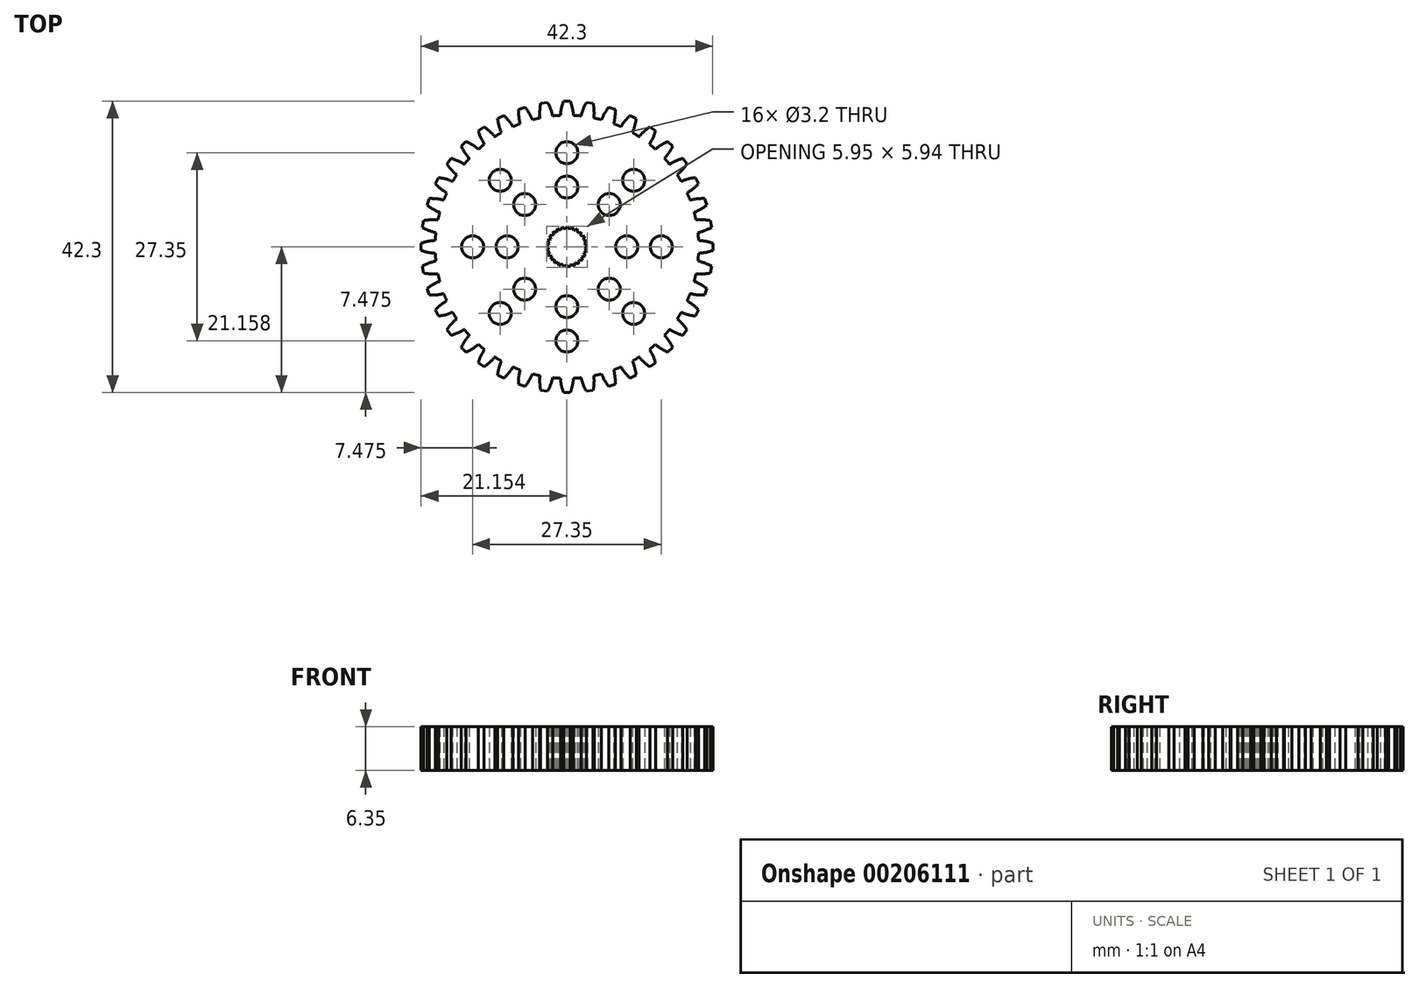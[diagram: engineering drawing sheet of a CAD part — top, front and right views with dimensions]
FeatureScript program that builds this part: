
annotation { "Feature Type Name" : "Feature", "Feature Type Description" : "" }
export const myFeature = defineFeature(function(context is Context, id is Id, definition is map)
    precondition{}
    {
        {
            var Q0;
            Q0=qCreatedBy(makeId("Top.planeOp"),FACE);
            var sketch = newSketch(context, id + "F0", { "sketchPlane" : qUnion([Q0])});
            skLineSegment(sketch, "E0", {"start": v(-0.5, 21.15) * mm, "end": v(0.5, 21.15) * mm});
            skArc(sketch, "E1", {"start": v(-0.5, 21.15) * mm, "mid": v(-0.8, 20.14) * mm, "end": v(-0.94, 19.09) * mm});
            skArc(sketch, "E2.MirrorCS", {"start": v(0.5, 21.15) * mm, "mid": v(0.8, 20.14) * mm, "end": v(0.94, 19.09) * mm});
            skPoint(sketch, "E3.center", {"position": v(0, 0) * mm});
            skLineSegment(sketch, "E4", {"start": v(-2.48, 1.65) * mm, "end": v(-2.31, 1.15) * mm});
            skLineSegment(sketch, "E5", {"start": v(-2.31, 1.15) * mm, "end": v(-2.81, 0.98) * mm});
            skLineSegment(sketch, "E6.1.0", {"start": v(-2.81, 0.98) * mm, "end": v(-2.53, 0.54) * mm});
            skLineSegment(sketch, "E6.1.1", {"start": v(-2.53, 0.54) * mm, "end": v(-2.97, 0.25) * mm});
            skLineSegment(sketch, "E6.2.0", {"start": v(-2.97, 0.25) * mm, "end": v(-2.58, -0.1) * mm});
            skLineSegment(sketch, "E6.2.1", {"start": v(-2.58, -0.1) * mm, "end": v(-2.94, -0.5) * mm});
            skLineSegment(sketch, "E6.3.0", {"start": v(-2.94, -0.5) * mm, "end": v(-2.47, -0.74) * mm});
            skLineSegment(sketch, "E6.3.1", {"start": v(-2.47, -0.74) * mm, "end": v(-2.72, -1.2) * mm});
            skLineSegment(sketch, "E6.4.0", {"start": v(-2.72, -1.2) * mm, "end": v(-2.21, -1.34) * mm});
            skLineSegment(sketch, "E6.4.1", {"start": v(-2.21, -1.34) * mm, "end": v(-2.34, -1.85) * mm});
            skLineSegment(sketch, "E6.5.0", {"start": v(-2.34, -1.85) * mm, "end": v(-1.8, -1.84) * mm});
            skLineSegment(sketch, "E6.5.1", {"start": v(-1.8, -1.84) * mm, "end": v(-1.8, -2.37) * mm});
            skLineSegment(sketch, "E6.6.0", {"start": v(-1.8, -2.37) * mm, "end": v(-1.3, -2.24) * mm});
            skLineSegment(sketch, "E6.6.1", {"start": v(-1.3, -2.24) * mm, "end": v(-1.16, -2.75) * mm});
            skLineSegment(sketch, "E6.7.0", {"start": v(-1.16, -2.75) * mm, "end": v(-0.7, -2.49) * mm});
            skLineSegment(sketch, "E6.7.1", {"start": v(-0.7, -2.49) * mm, "end": v(-0.44, -2.95) * mm});
            skLineSegment(sketch, "E6.8.0", {"start": v(-0.44, -2.95) * mm, "end": v(-0.06, -2.58) * mm});
            skLineSegment(sketch, "E6.8.1", {"start": v(-0.06, -2.58) * mm, "end": v(0.3, -2.96) * mm});
            skLineSegment(sketch, "E6.9.0", {"start": v(0.3, -2.96) * mm, "end": v(0.59, -2.52) * mm});
            skLineSegment(sketch, "E6.9.1", {"start": v(0.59, -2.52) * mm, "end": v(1.04, -2.8) * mm});
            skLineSegment(sketch, "E6.10.0", {"start": v(1.04, -2.8) * mm, "end": v(1.2, -2.3) * mm});
            skLineSegment(sketch, "E6.10.1", {"start": v(1.2, -2.3) * mm, "end": v(1.7, -2.45) * mm});
            skLineSegment(sketch, "E6.11.0", {"start": v(1.7, -2.45) * mm, "end": v(1.73, -1.92) * mm});
            skLineSegment(sketch, "E6.11.1", {"start": v(1.73, -1.92) * mm, "end": v(2.25, -1.95) * mm});
            skLineSegment(sketch, "E6.12.0", {"start": v(2.25, -1.95) * mm, "end": v(2.15, -1.43) * mm});
            skLineSegment(sketch, "E6.12.1", {"start": v(2.15, -1.43) * mm, "end": v(2.67, -1.33) * mm});
            skLineSegment(sketch, "E6.13.0", {"start": v(2.67, -1.33) * mm, "end": v(2.44, -0.85) * mm});
            skLineSegment(sketch, "E6.13.1", {"start": v(2.44, -0.85) * mm, "end": v(2.91, -0.62) * mm});
            skLineSegment(sketch, "E6.14.0", {"start": v(2.91, -0.62) * mm, "end": v(2.57, -0.22) * mm});
            skLineSegment(sketch, "E6.14.1", {"start": v(2.57, -0.22) * mm, "end": v(2.98, 0.12) * mm});
            skLineSegment(sketch, "E6.15.0", {"start": v(2.98, 0.12) * mm, "end": v(2.55, 0.43) * mm});
            skLineSegment(sketch, "E6.15.1", {"start": v(2.55, 0.43) * mm, "end": v(2.85, 0.86) * mm});
            skLineSegment(sketch, "E6.16.0", {"start": v(2.85, 0.86) * mm, "end": v(2.36, 1.05) * mm});
            skLineSegment(sketch, "E6.16.1", {"start": v(2.36, 1.05) * mm, "end": v(2.55, 1.54) * mm});
            skLineSegment(sketch, "E6.17.0", {"start": v(2.55, 1.54) * mm, "end": v(2.03, 1.6) * mm});
            skLineSegment(sketch, "E6.17.1", {"start": v(2.03, 1.6) * mm, "end": v(2.09, 2.13) * mm});
            skLineSegment(sketch, "E6.18.0", {"start": v(2.09, 2.13) * mm, "end": v(1.56, 2.06) * mm});
            skLineSegment(sketch, "E6.18.1", {"start": v(1.56, 2.06) * mm, "end": v(1.5, 2.58) * mm});
            skLineSegment(sketch, "E6.19.0", {"start": v(1.5, 2.58) * mm, "end": v(1, 2.38) * mm});
            skLineSegment(sketch, "E6.19.1", {"start": v(1, 2.38) * mm, "end": v(0.8, 2.87) * mm});
            skLineSegment(sketch, "E6.20.0", {"start": v(0.8, 2.87) * mm, "end": v(0.38, 2.56) * mm});
            skLineSegment(sketch, "E6.20.1", {"start": v(0.38, 2.56) * mm, "end": v(0.07, 2.98) * mm});
            skLineSegment(sketch, "E6.21.0", {"start": v(0.07, 2.98) * mm, "end": v(-0.27, 2.57) * mm});
            skLineSegment(sketch, "E6.21.1", {"start": v(-0.27, 2.57) * mm, "end": v(-0.68, 2.9) * mm});
            skLineSegment(sketch, "E6.22.0", {"start": v(-0.68, 2.9) * mm, "end": v(-0.9, 2.42) * mm});
            skLineSegment(sketch, "E6.22.1", {"start": v(-0.9, 2.42) * mm, "end": v(-1.38, 2.64) * mm});
            skLineSegment(sketch, "E6.23.0", {"start": v(-1.38, 2.64) * mm, "end": v(-1.47, 2.12) * mm});
            skLineSegment(sketch, "E6.23.1", {"start": v(-1.47, 2.12) * mm, "end": v(-2, 2.22) * mm});
            skLineSegment(sketch, "E6.24.0", {"start": v(-2, 2.22) * mm, "end": v(-1.95, 1.69) * mm});
            skLineSegment(sketch, "E6.24.1", {"start": v(-1.95, 1.69) * mm, "end": v(-2.48, 1.65) * mm});
            skCircle(sketch, "E7", {"center": v(0, 13.67) * mm, "radius": 1.6 * mm});
            skCircle(sketch, "E8", {"center": v(0, 8.67) * mm, "radius": 1.6 * mm});
            skLineSegment(sketch, "E9", {"start": v(0, 13.67) * mm, "end": v(0, 7.54) * mm});
            skCircle(sketch, "E10.1.0", {"center": v(-9.67, 9.67) * mm, "radius": 1.6 * mm});
            skCircle(sketch, "E10.1.1", {"center": v(-6.13, 6.13) * mm, "radius": 1.6 * mm});
            skCircle(sketch, "E10.2.0", {"center": v(-13.67, 0) * mm, "radius": 1.6 * mm});
            skCircle(sketch, "E10.2.1", {"center": v(-8.67, 0) * mm, "radius": 1.6 * mm});
            skCircle(sketch, "E10.3.0", {"center": v(-9.67, -9.67) * mm, "radius": 1.6 * mm});
            skCircle(sketch, "E10.3.1", {"center": v(-6.13, -6.13) * mm, "radius": 1.6 * mm});
            skCircle(sketch, "E10.4.0", {"center": v(0, -13.67) * mm, "radius": 1.6 * mm});
            skCircle(sketch, "E10.4.1", {"center": v(0, -8.67) * mm, "radius": 1.6 * mm});
            skCircle(sketch, "E10.5.0", {"center": v(9.67, -9.67) * mm, "radius": 1.6 * mm});
            skCircle(sketch, "E10.5.1", {"center": v(6.13, -6.13) * mm, "radius": 1.6 * mm});
            skCircle(sketch, "E10.6.0", {"center": v(13.67, 0) * mm, "radius": 1.6 * mm});
            skCircle(sketch, "E10.6.1", {"center": v(8.67, 0) * mm, "radius": 1.6 * mm});
            skCircle(sketch, "E10.7.0", {"center": v(9.67, 9.67) * mm, "radius": 1.6 * mm});
            skCircle(sketch, "E10.7.1", {"center": v(6.13, 6.13) * mm, "radius": 1.6 * mm});
            skArc(sketch, "E11", {"start": v(2.06, 19) * mm, "mid": v(1.5, 19.05) * mm, "end": v(0.94, 19.09) * mm});
            skArc(sketch, "E12.1.0", {"start": v(-2.81, 20.97) * mm, "mid": v(-2.36, 20.01) * mm, "end": v(-2.06, 19) * mm});
            skLineSegment(sketch, "E12.1.1", {"start": v(-3.8, 20.81) * mm, "end": v(-2.81, 20.97) * mm});
            skArc(sketch, "E12.1.2", {"start": v(-3.8, 20.81) * mm, "mid": v(-3.93, 19.76) * mm, "end": v(-3.91, 18.7) * mm});
            skArc(sketch, "E12.1.3", {"start": v(-0.94, 19.09) * mm, "mid": v(-1.5, 19.05) * mm, "end": v(-2.06, 19) * mm});
            skArc(sketch, "E12.2.0", {"start": v(-6.06, 20.27) * mm, "mid": v(-5.47, 19.4) * mm, "end": v(-5, 18.44) * mm});
            skLineSegment(sketch, "E12.2.1", {"start": v(-7.01, 19.96) * mm, "end": v(-6.06, 20.27) * mm});
            skArc(sketch, "E12.2.2", {"start": v(-7.01, 19.96) * mm, "mid": v(-6.98, 18.9) * mm, "end": v(-6.79, 17.86) * mm});
            skArc(sketch, "E12.2.3", {"start": v(-3.91, 18.7) * mm, "mid": v(-4.46, 18.58) * mm, "end": v(-5, 18.44) * mm});
            skArc(sketch, "E12.3.0", {"start": v(-9.16, 19.07) * mm, "mid": v(-8.43, 18.3) * mm, "end": v(-7.83, 17.43) * mm});
            skLineSegment(sketch, "E12.3.1", {"start": v(-10.05, 18.62) * mm, "end": v(-9.16, 19.07) * mm});
            skArc(sketch, "E12.3.2", {"start": v(-10.05, 18.62) * mm, "mid": v(-9.85, 17.58) * mm, "end": v(-9.5, 16.58) * mm});
            skArc(sketch, "E12.3.3", {"start": v(-6.79, 17.86) * mm, "mid": v(-7.31, 17.66) * mm, "end": v(-7.83, 17.43) * mm});
            skArc(sketch, "E12.4.0", {"start": v(-12.03, 17.4) * mm, "mid": v(-11.2, 16.76) * mm, "end": v(-10.46, 16) * mm});
            skLineSegment(sketch, "E12.4.1", {"start": v(-12.84, 16.82) * mm, "end": v(-12.03, 17.4) * mm});
            skArc(sketch, "E12.4.2", {"start": v(-12.84, 16.82) * mm, "mid": v(-12.48, 15.82) * mm, "end": v(-11.98, 14.9) * mm});
            skArc(sketch, "E12.4.3", {"start": v(-9.5, 16.58) * mm, "mid": v(-9.98, 16.3) * mm, "end": v(-10.46, 16) * mm});
            skArc(sketch, "E12.5.0", {"start": v(-14.6, 15.3) * mm, "mid": v(-13.68, 14.8) * mm, "end": v(-12.83, 14.16) * mm});
            skLineSegment(sketch, "E12.5.1", {"start": v(-15.3, 14.6) * mm, "end": v(-14.6, 15.3) * mm});
            skArc(sketch, "E12.5.2", {"start": v(-15.3, 14.6) * mm, "mid": v(-14.8, 13.68) * mm, "end": v(-14.16, 12.83) * mm});
            skArc(sketch, "E12.5.3", {"start": v(-11.98, 14.9) * mm, "mid": v(-12.41, 14.53) * mm, "end": v(-12.83, 14.16) * mm});
            skArc(sketch, "E12.6.0", {"start": v(-16.82, 12.84) * mm, "mid": v(-15.82, 12.48) * mm, "end": v(-14.9, 11.98) * mm});
            skLineSegment(sketch, "E12.6.1", {"start": v(-17.4, 12.03) * mm, "end": v(-16.82, 12.84) * mm});
            skArc(sketch, "E12.6.2", {"start": v(-17.4, 12.03) * mm, "mid": v(-16.76, 11.2) * mm, "end": v(-16, 10.46) * mm});
            skArc(sketch, "E12.6.3", {"start": v(-14.16, 12.83) * mm, "mid": v(-14.53, 12.41) * mm, "end": v(-14.9, 11.98) * mm});
            skArc(sketch, "E12.7.0", {"start": v(-18.62, 10.05) * mm, "mid": v(-17.58, 9.85) * mm, "end": v(-16.58, 9.5) * mm});
            skLineSegment(sketch, "E12.7.1", {"start": v(-19.07, 9.16) * mm, "end": v(-18.62, 10.05) * mm});
            skArc(sketch, "E12.7.2", {"start": v(-19.07, 9.16) * mm, "mid": v(-18.3, 8.43) * mm, "end": v(-17.43, 7.83) * mm});
            skArc(sketch, "E12.7.3", {"start": v(-16, 10.46) * mm, "mid": v(-16.3, 9.98) * mm, "end": v(-16.58, 9.5) * mm});
            skArc(sketch, "E12.8.0", {"start": v(-19.96, 7.01) * mm, "mid": v(-18.9, 6.98) * mm, "end": v(-17.86, 6.79) * mm});
            skLineSegment(sketch, "E12.8.1", {"start": v(-20.27, 6.06) * mm, "end": v(-19.96, 7.01) * mm});
            skArc(sketch, "E12.8.2", {"start": v(-20.27, 6.06) * mm, "mid": v(-19.4, 5.47) * mm, "end": v(-18.44, 5) * mm});
            skArc(sketch, "E12.8.3", {"start": v(-17.43, 7.83) * mm, "mid": v(-17.66, 7.31) * mm, "end": v(-17.86, 6.79) * mm});
            skArc(sketch, "E12.9.0", {"start": v(-20.81, 3.8) * mm, "mid": v(-19.76, 3.93) * mm, "end": v(-18.7, 3.91) * mm});
            skLineSegment(sketch, "E12.9.1", {"start": v(-20.97, 2.81) * mm, "end": v(-20.81, 3.8) * mm});
            skArc(sketch, "E12.9.2", {"start": v(-20.97, 2.81) * mm, "mid": v(-20.01, 2.36) * mm, "end": v(-19, 2.06) * mm});
            skArc(sketch, "E12.9.3", {"start": v(-18.44, 5) * mm, "mid": v(-18.58, 4.46) * mm, "end": v(-18.7, 3.91) * mm});
            skArc(sketch, "E12.10.0", {"start": v(-21.15, 0.5) * mm, "mid": v(-20.14, 0.8) * mm, "end": v(-19.09, 0.94) * mm});
            skLineSegment(sketch, "E12.10.1", {"start": v(-21.15, -0.5) * mm, "end": v(-21.15, 0.5) * mm});
            skArc(sketch, "E12.10.2", {"start": v(-21.15, -0.5) * mm, "mid": v(-20.14, -0.8) * mm, "end": v(-19.09, -0.94) * mm});
            skArc(sketch, "E12.10.3", {"start": v(-19, 2.06) * mm, "mid": v(-19.05, 1.5) * mm, "end": v(-19.09, 0.94) * mm});
            skArc(sketch, "E12.11.0", {"start": v(-20.97, -2.81) * mm, "mid": v(-20.01, -2.36) * mm, "end": v(-19, -2.06) * mm});
            skLineSegment(sketch, "E12.11.1", {"start": v(-20.81, -3.8) * mm, "end": v(-20.97, -2.81) * mm});
            skArc(sketch, "E12.11.2", {"start": v(-20.81, -3.8) * mm, "mid": v(-19.76, -3.93) * mm, "end": v(-18.7, -3.91) * mm});
            skArc(sketch, "E12.11.3", {"start": v(-19.09, -0.94) * mm, "mid": v(-19.05, -1.5) * mm, "end": v(-19, -2.06) * mm});
            skArc(sketch, "E12.12.0", {"start": v(-20.27, -6.06) * mm, "mid": v(-19.4, -5.47) * mm, "end": v(-18.44, -5) * mm});
            skLineSegment(sketch, "E12.12.1", {"start": v(-19.96, -7.01) * mm, "end": v(-20.27, -6.06) * mm});
            skArc(sketch, "E12.12.2", {"start": v(-19.96, -7.01) * mm, "mid": v(-18.9, -6.98) * mm, "end": v(-17.86, -6.79) * mm});
            skArc(sketch, "E12.12.3", {"start": v(-18.7, -3.91) * mm, "mid": v(-18.58, -4.46) * mm, "end": v(-18.44, -5) * mm});
            skArc(sketch, "E12.13.0", {"start": v(-19.07, -9.16) * mm, "mid": v(-18.3, -8.43) * mm, "end": v(-17.43, -7.83) * mm});
            skLineSegment(sketch, "E12.13.1", {"start": v(-18.62, -10.05) * mm, "end": v(-19.07, -9.16) * mm});
            skArc(sketch, "E12.13.2", {"start": v(-18.62, -10.05) * mm, "mid": v(-17.58, -9.85) * mm, "end": v(-16.58, -9.5) * mm});
            skArc(sketch, "E12.13.3", {"start": v(-17.86, -6.79) * mm, "mid": v(-17.66, -7.31) * mm, "end": v(-17.43, -7.83) * mm});
            skArc(sketch, "E12.14.0", {"start": v(-17.4, -12.03) * mm, "mid": v(-16.76, -11.2) * mm, "end": v(-16, -10.46) * mm});
            skLineSegment(sketch, "E12.14.1", {"start": v(-16.82, -12.84) * mm, "end": v(-17.4, -12.03) * mm});
            skArc(sketch, "E12.14.2", {"start": v(-16.82, -12.84) * mm, "mid": v(-15.82, -12.48) * mm, "end": v(-14.9, -11.98) * mm});
            skArc(sketch, "E12.14.3", {"start": v(-16.58, -9.5) * mm, "mid": v(-16.3, -9.98) * mm, "end": v(-16, -10.46) * mm});
            skArc(sketch, "E12.15.0", {"start": v(-15.3, -14.6) * mm, "mid": v(-14.8, -13.68) * mm, "end": v(-14.16, -12.83) * mm});
            skLineSegment(sketch, "E12.15.1", {"start": v(-14.6, -15.3) * mm, "end": v(-15.3, -14.6) * mm});
            skArc(sketch, "E12.15.2", {"start": v(-14.6, -15.3) * mm, "mid": v(-13.68, -14.8) * mm, "end": v(-12.83, -14.16) * mm});
            skArc(sketch, "E12.15.3", {"start": v(-14.9, -11.98) * mm, "mid": v(-14.53, -12.41) * mm, "end": v(-14.16, -12.83) * mm});
            skArc(sketch, "E12.16.0", {"start": v(-12.84, -16.82) * mm, "mid": v(-12.48, -15.82) * mm, "end": v(-11.98, -14.9) * mm});
            skLineSegment(sketch, "E12.16.1", {"start": v(-12.03, -17.4) * mm, "end": v(-12.84, -16.82) * mm});
            skArc(sketch, "E12.16.2", {"start": v(-12.03, -17.4) * mm, "mid": v(-11.2, -16.76) * mm, "end": v(-10.46, -16) * mm});
            skArc(sketch, "E12.16.3", {"start": v(-12.83, -14.16) * mm, "mid": v(-12.41, -14.53) * mm, "end": v(-11.98, -14.9) * mm});
            skArc(sketch, "E12.17.0", {"start": v(-10.05, -18.62) * mm, "mid": v(-9.85, -17.58) * mm, "end": v(-9.5, -16.58) * mm});
            skLineSegment(sketch, "E12.17.1", {"start": v(-9.16, -19.07) * mm, "end": v(-10.05, -18.62) * mm});
            skArc(sketch, "E12.17.2", {"start": v(-9.16, -19.07) * mm, "mid": v(-8.43, -18.3) * mm, "end": v(-7.83, -17.43) * mm});
            skArc(sketch, "E12.17.3", {"start": v(-10.46, -16) * mm, "mid": v(-9.98, -16.3) * mm, "end": v(-9.5, -16.58) * mm});
            skArc(sketch, "E12.18.0", {"start": v(-7.01, -19.96) * mm, "mid": v(-6.98, -18.9) * mm, "end": v(-6.79, -17.86) * mm});
            skLineSegment(sketch, "E12.18.1", {"start": v(-6.06, -20.27) * mm, "end": v(-7.01, -19.96) * mm});
            skArc(sketch, "E12.18.2", {"start": v(-6.06, -20.27) * mm, "mid": v(-5.47, -19.4) * mm, "end": v(-5, -18.44) * mm});
            skArc(sketch, "E12.18.3", {"start": v(-7.83, -17.43) * mm, "mid": v(-7.31, -17.66) * mm, "end": v(-6.79, -17.86) * mm});
            skArc(sketch, "E12.19.0", {"start": v(-3.8, -20.81) * mm, "mid": v(-3.93, -19.76) * mm, "end": v(-3.91, -18.7) * mm});
            skLineSegment(sketch, "E12.19.1", {"start": v(-2.81, -20.97) * mm, "end": v(-3.8, -20.81) * mm});
            skArc(sketch, "E12.19.2", {"start": v(-2.81, -20.97) * mm, "mid": v(-2.36, -20.01) * mm, "end": v(-2.06, -19) * mm});
            skArc(sketch, "E12.19.3", {"start": v(-5, -18.44) * mm, "mid": v(-4.46, -18.58) * mm, "end": v(-3.91, -18.7) * mm});
            skArc(sketch, "E12.20.0", {"start": v(-0.5, -21.15) * mm, "mid": v(-0.8, -20.14) * mm, "end": v(-0.94, -19.09) * mm});
            skLineSegment(sketch, "E12.20.1", {"start": v(0.5, -21.15) * mm, "end": v(-0.5, -21.15) * mm});
            skArc(sketch, "E12.20.2", {"start": v(0.5, -21.15) * mm, "mid": v(0.8, -20.14) * mm, "end": v(0.94, -19.09) * mm});
            skArc(sketch, "E12.20.3", {"start": v(-2.06, -19) * mm, "mid": v(-1.5, -19.05) * mm, "end": v(-0.94, -19.09) * mm});
            skArc(sketch, "E12.21.0", {"start": v(2.81, -20.97) * mm, "mid": v(2.36, -20.01) * mm, "end": v(2.06, -19) * mm});
            skLineSegment(sketch, "E12.21.1", {"start": v(3.8, -20.81) * mm, "end": v(2.81, -20.97) * mm});
            skArc(sketch, "E12.21.2", {"start": v(3.8, -20.81) * mm, "mid": v(3.93, -19.76) * mm, "end": v(3.91, -18.7) * mm});
            skArc(sketch, "E12.21.3", {"start": v(0.94, -19.09) * mm, "mid": v(1.5, -19.05) * mm, "end": v(2.06, -19) * mm});
            skArc(sketch, "E12.22.0", {"start": v(6.06, -20.27) * mm, "mid": v(5.47, -19.4) * mm, "end": v(5, -18.44) * mm});
            skLineSegment(sketch, "E12.22.1", {"start": v(7.01, -19.96) * mm, "end": v(6.06, -20.27) * mm});
            skArc(sketch, "E12.22.2", {"start": v(7.01, -19.96) * mm, "mid": v(6.98, -18.9) * mm, "end": v(6.79, -17.86) * mm});
            skArc(sketch, "E12.22.3", {"start": v(3.91, -18.7) * mm, "mid": v(4.46, -18.58) * mm, "end": v(5, -18.44) * mm});
            skArc(sketch, "E12.23.0", {"start": v(9.16, -19.07) * mm, "mid": v(8.43, -18.3) * mm, "end": v(7.83, -17.43) * mm});
            skLineSegment(sketch, "E12.23.1", {"start": v(10.05, -18.62) * mm, "end": v(9.16, -19.07) * mm});
            skArc(sketch, "E12.23.2", {"start": v(10.05, -18.62) * mm, "mid": v(9.85, -17.58) * mm, "end": v(9.5, -16.58) * mm});
            skArc(sketch, "E12.23.3", {"start": v(6.79, -17.86) * mm, "mid": v(7.31, -17.66) * mm, "end": v(7.83, -17.43) * mm});
            skArc(sketch, "E12.24.0", {"start": v(12.03, -17.4) * mm, "mid": v(11.2, -16.76) * mm, "end": v(10.46, -16) * mm});
            skLineSegment(sketch, "E12.24.1", {"start": v(12.84, -16.82) * mm, "end": v(12.03, -17.4) * mm});
            skArc(sketch, "E12.24.2", {"start": v(12.84, -16.82) * mm, "mid": v(12.48, -15.82) * mm, "end": v(11.98, -14.9) * mm});
            skArc(sketch, "E12.24.3", {"start": v(9.5, -16.58) * mm, "mid": v(9.98, -16.3) * mm, "end": v(10.46, -16) * mm});
            skArc(sketch, "E12.25.0", {"start": v(14.6, -15.3) * mm, "mid": v(13.68, -14.8) * mm, "end": v(12.83, -14.16) * mm});
            skLineSegment(sketch, "E12.25.1", {"start": v(15.3, -14.6) * mm, "end": v(14.6, -15.3) * mm});
            skArc(sketch, "E12.25.2", {"start": v(15.3, -14.6) * mm, "mid": v(14.8, -13.68) * mm, "end": v(14.16, -12.83) * mm});
            skArc(sketch, "E12.25.3", {"start": v(11.98, -14.9) * mm, "mid": v(12.41, -14.53) * mm, "end": v(12.83, -14.16) * mm});
            skArc(sketch, "E12.26.0", {"start": v(16.82, -12.84) * mm, "mid": v(15.82, -12.48) * mm, "end": v(14.9, -11.98) * mm});
            skLineSegment(sketch, "E12.26.1", {"start": v(17.4, -12.03) * mm, "end": v(16.82, -12.84) * mm});
            skArc(sketch, "E12.26.2", {"start": v(17.4, -12.03) * mm, "mid": v(16.76, -11.2) * mm, "end": v(16, -10.46) * mm});
            skArc(sketch, "E12.26.3", {"start": v(14.16, -12.83) * mm, "mid": v(14.53, -12.41) * mm, "end": v(14.9, -11.98) * mm});
            skArc(sketch, "E12.27.0", {"start": v(18.62, -10.05) * mm, "mid": v(17.58, -9.85) * mm, "end": v(16.58, -9.5) * mm});
            skLineSegment(sketch, "E12.27.1", {"start": v(19.07, -9.16) * mm, "end": v(18.62, -10.05) * mm});
            skArc(sketch, "E12.27.2", {"start": v(19.07, -9.16) * mm, "mid": v(18.3, -8.43) * mm, "end": v(17.43, -7.83) * mm});
            skArc(sketch, "E12.27.3", {"start": v(16, -10.46) * mm, "mid": v(16.3, -9.98) * mm, "end": v(16.58, -9.5) * mm});
            skArc(sketch, "E12.28.0", {"start": v(19.96, -7.01) * mm, "mid": v(18.9, -6.98) * mm, "end": v(17.86, -6.79) * mm});
            skLineSegment(sketch, "E12.28.1", {"start": v(20.27, -6.06) * mm, "end": v(19.96, -7.01) * mm});
            skArc(sketch, "E12.28.2", {"start": v(20.27, -6.06) * mm, "mid": v(19.4, -5.47) * mm, "end": v(18.44, -5) * mm});
            skArc(sketch, "E12.28.3", {"start": v(17.43, -7.83) * mm, "mid": v(17.66, -7.31) * mm, "end": v(17.86, -6.79) * mm});
            skArc(sketch, "E12.29.0", {"start": v(20.81, -3.8) * mm, "mid": v(19.76, -3.93) * mm, "end": v(18.7, -3.91) * mm});
            skLineSegment(sketch, "E12.29.1", {"start": v(20.97, -2.81) * mm, "end": v(20.81, -3.8) * mm});
            skArc(sketch, "E12.29.2", {"start": v(20.97, -2.81) * mm, "mid": v(20.01, -2.36) * mm, "end": v(19, -2.06) * mm});
            skArc(sketch, "E12.29.3", {"start": v(18.44, -5) * mm, "mid": v(18.58, -4.46) * mm, "end": v(18.7, -3.91) * mm});
            skArc(sketch, "E12.30.0", {"start": v(21.15, -0.5) * mm, "mid": v(20.14, -0.8) * mm, "end": v(19.09, -0.94) * mm});
            skLineSegment(sketch, "E12.30.1", {"start": v(21.15, 0.5) * mm, "end": v(21.15, -0.5) * mm});
            skArc(sketch, "E12.30.2", {"start": v(21.15, 0.5) * mm, "mid": v(20.14, 0.8) * mm, "end": v(19.09, 0.94) * mm});
            skArc(sketch, "E12.30.3", {"start": v(19, -2.06) * mm, "mid": v(19.05, -1.5) * mm, "end": v(19.09, -0.94) * mm});
            skArc(sketch, "E12.31.0", {"start": v(20.97, 2.81) * mm, "mid": v(20.01, 2.36) * mm, "end": v(19, 2.06) * mm});
            skLineSegment(sketch, "E12.31.1", {"start": v(20.81, 3.8) * mm, "end": v(20.97, 2.81) * mm});
            skArc(sketch, "E12.31.2", {"start": v(20.81, 3.8) * mm, "mid": v(19.76, 3.93) * mm, "end": v(18.7, 3.91) * mm});
            skArc(sketch, "E12.31.3", {"start": v(19.09, 0.94) * mm, "mid": v(19.05, 1.5) * mm, "end": v(19, 2.06) * mm});
            skArc(sketch, "E12.32.0", {"start": v(20.27, 6.06) * mm, "mid": v(19.4, 5.47) * mm, "end": v(18.44, 5) * mm});
            skLineSegment(sketch, "E12.32.1", {"start": v(19.96, 7.01) * mm, "end": v(20.27, 6.06) * mm});
            skArc(sketch, "E12.32.2", {"start": v(19.96, 7.01) * mm, "mid": v(18.9, 6.98) * mm, "end": v(17.86, 6.79) * mm});
            skArc(sketch, "E12.32.3", {"start": v(18.7, 3.91) * mm, "mid": v(18.58, 4.46) * mm, "end": v(18.44, 5) * mm});
            skArc(sketch, "E12.33.0", {"start": v(19.07, 9.16) * mm, "mid": v(18.3, 8.43) * mm, "end": v(17.43, 7.83) * mm});
            skLineSegment(sketch, "E12.33.1", {"start": v(18.62, 10.05) * mm, "end": v(19.07, 9.16) * mm});
            skArc(sketch, "E12.33.2", {"start": v(18.62, 10.05) * mm, "mid": v(17.58, 9.85) * mm, "end": v(16.58, 9.5) * mm});
            skArc(sketch, "E12.33.3", {"start": v(17.86, 6.79) * mm, "mid": v(17.66, 7.31) * mm, "end": v(17.43, 7.83) * mm});
            skArc(sketch, "E12.34.0", {"start": v(17.4, 12.03) * mm, "mid": v(16.76, 11.2) * mm, "end": v(16, 10.46) * mm});
            skLineSegment(sketch, "E12.34.1", {"start": v(16.82, 12.84) * mm, "end": v(17.4, 12.03) * mm});
            skArc(sketch, "E12.34.2", {"start": v(16.82, 12.84) * mm, "mid": v(15.82, 12.48) * mm, "end": v(14.9, 11.98) * mm});
            skArc(sketch, "E12.34.3", {"start": v(16.58, 9.5) * mm, "mid": v(16.3, 9.98) * mm, "end": v(16, 10.46) * mm});
            skArc(sketch, "E12.35.0", {"start": v(15.3, 14.6) * mm, "mid": v(14.8, 13.68) * mm, "end": v(14.16, 12.83) * mm});
            skLineSegment(sketch, "E12.35.1", {"start": v(14.6, 15.3) * mm, "end": v(15.3, 14.6) * mm});
            skArc(sketch, "E12.35.2", {"start": v(14.6, 15.3) * mm, "mid": v(13.68, 14.8) * mm, "end": v(12.83, 14.16) * mm});
            skArc(sketch, "E12.35.3", {"start": v(14.9, 11.98) * mm, "mid": v(14.53, 12.41) * mm, "end": v(14.16, 12.83) * mm});
            skArc(sketch, "E12.36.0", {"start": v(12.84, 16.82) * mm, "mid": v(12.48, 15.82) * mm, "end": v(11.98, 14.9) * mm});
            skLineSegment(sketch, "E12.36.1", {"start": v(12.03, 17.4) * mm, "end": v(12.84, 16.82) * mm});
            skArc(sketch, "E12.36.2", {"start": v(12.03, 17.4) * mm, "mid": v(11.2, 16.76) * mm, "end": v(10.46, 16) * mm});
            skArc(sketch, "E12.36.3", {"start": v(12.83, 14.16) * mm, "mid": v(12.41, 14.53) * mm, "end": v(11.98, 14.9) * mm});
            skArc(sketch, "E12.37.0", {"start": v(10.05, 18.62) * mm, "mid": v(9.85, 17.58) * mm, "end": v(9.5, 16.58) * mm});
            skLineSegment(sketch, "E12.37.1", {"start": v(9.16, 19.07) * mm, "end": v(10.05, 18.62) * mm});
            skArc(sketch, "E12.37.2", {"start": v(9.16, 19.07) * mm, "mid": v(8.43, 18.3) * mm, "end": v(7.83, 17.43) * mm});
            skArc(sketch, "E12.37.3", {"start": v(10.46, 16) * mm, "mid": v(9.98, 16.3) * mm, "end": v(9.5, 16.58) * mm});
            skArc(sketch, "E12.38.0", {"start": v(7.01, 19.96) * mm, "mid": v(6.98, 18.9) * mm, "end": v(6.79, 17.86) * mm});
            skLineSegment(sketch, "E12.38.1", {"start": v(6.06, 20.27) * mm, "end": v(7.01, 19.96) * mm});
            skArc(sketch, "E12.38.2", {"start": v(6.06, 20.27) * mm, "mid": v(5.47, 19.4) * mm, "end": v(5, 18.44) * mm});
            skArc(sketch, "E12.38.3", {"start": v(7.83, 17.43) * mm, "mid": v(7.31, 17.66) * mm, "end": v(6.79, 17.86) * mm});
            skArc(sketch, "E12.39.0", {"start": v(3.8, 20.81) * mm, "mid": v(3.93, 19.76) * mm, "end": v(3.91, 18.7) * mm});
            skLineSegment(sketch, "E12.39.1", {"start": v(2.81, 20.97) * mm, "end": v(3.8, 20.81) * mm});
            skArc(sketch, "E12.39.2", {"start": v(2.81, 20.97) * mm, "mid": v(2.36, 20.01) * mm, "end": v(2.06, 19) * mm});
            skArc(sketch, "E12.39.3", {"start": v(5, 18.44) * mm, "mid": v(4.46, 18.58) * mm, "end": v(3.91, 18.7) * mm});
            skSolve(sketch);
        }
        {
            var Q0;
            Q0=makeQuery(id+"F0.imprint","IMPRINT",FACE,{"disambiguationData":[TD([[makeQuery(id+"F0.imprint","IMPRINT",EDGE,{"derivedFrom":sQuery(id+"F0.wireOp",EDGE,"E0")}),-1.0]])]});
            extrude(context, id + "F1", {"entities" : qUnion([Q0]), "depth" : 6.35 * mm});
        }
    });
